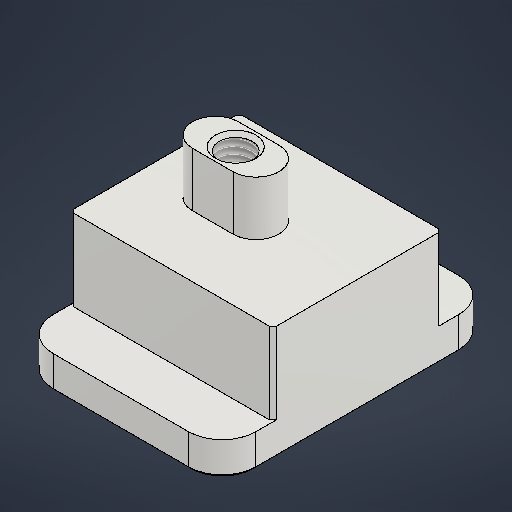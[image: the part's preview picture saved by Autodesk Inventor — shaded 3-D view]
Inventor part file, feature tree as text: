
AUTODESK INVENTOR PART (.ipt)
format: ipt  version: 2025.3 (Build 293356000, 356)  size: 249,856 bytes
history: native  units: mm
features: extrude x4, sketch x2, hole x1, fillet x1, chamfer x1
ambient origin geometry x8: Origin, YZ Plane, XZ Plane, XY Plane, X Axis, Y Axis, Z Axis, Center Point
bodies: Solid1 (feature_tree)
feature tree (9):
  sketch  "Sketch1"  dims[d0=40.0mm d1=30.0mm]
  extrude  "Extrusion1"  Depth=30.0mm
  extrude  "Extrusion2"  Depth=6.8mm
  extrude  "Extrusion5"  Depth=25.0mm
  extrude  "Extrusion6"  TaperAngle=0.0deg  [1 undecoded]
  hole  "Hole1"  [1 undecoded]
  fillet  "Fillet1"  [1 undecoded]
  chamfer  "Chamfer1"  Distance=10.0mm
  sketch  "Sketch3"  dims[d2=6.0mm d3=6.8mm d4=25.0mm d5=0.0mm d6=8.0mm d7=0.0mm d8=4.917mm d9=10.0mm d10=6.0mm d11=2.0mm d12=90.0deg d13=15.0mm d14=0.0mm d15=5.0mm d16=0.5mm d17=2.0mm d18=45.0deg d19=3.0mm d29=15.0mm d30=12.0mm d31=0.0mm d35=25.0mm d36=20.0mm d37=0.0mm]
note: 3 required parameter values undecoded (feature->parameter linkage not recoverable at this tier; creation-order binding heuristic only, values carry confidence <= 0.55)
